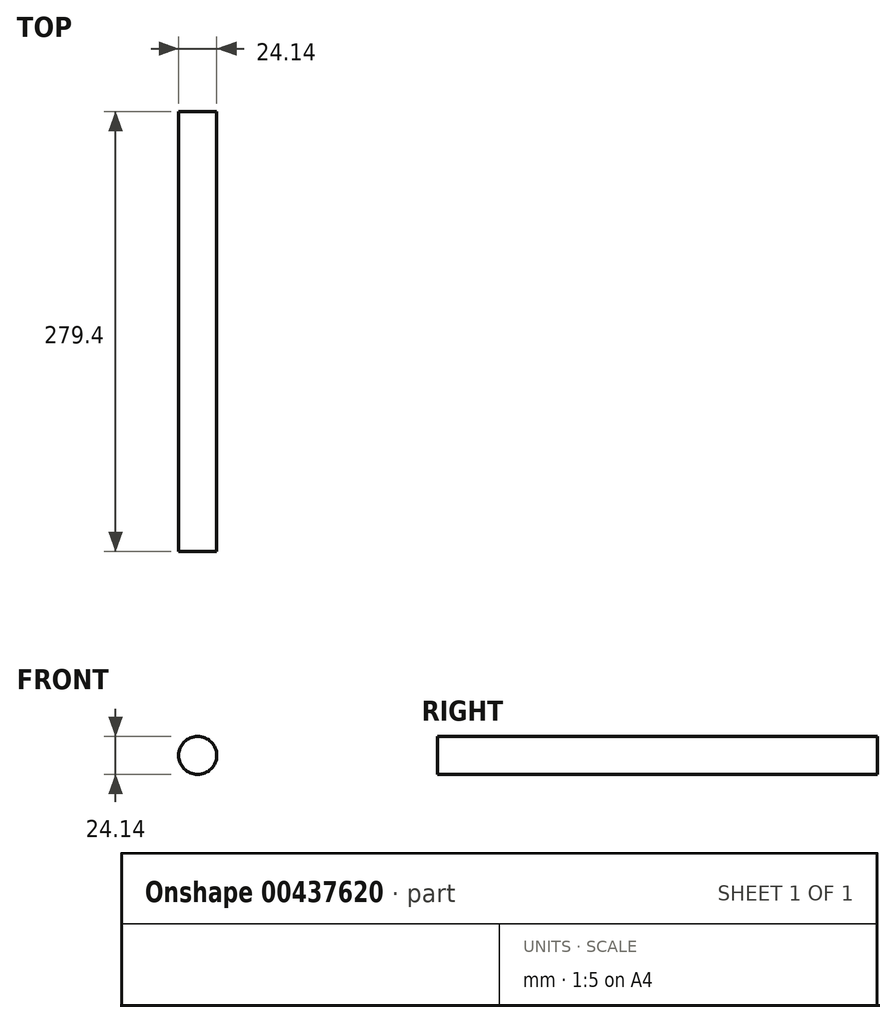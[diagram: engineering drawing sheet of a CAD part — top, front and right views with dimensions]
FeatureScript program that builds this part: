
annotation { "Feature Type Name" : "Feature", "Feature Type Description" : "" }
export const myFeature = defineFeature(function(context is Context, id is Id, definition is map)
    precondition{}
    {
        {
            var Q0;
            Q0=qCreatedBy(makeId("Front.planeOp"),FACE);
            var sketch = newSketch(context, id + "F0", { "sketchPlane" : qUnion([Q0])});
            skCircle(sketch, "E0", {"center": v(0, 0) * mm, "radius": 12.07 * mm});
            skSolve(sketch);
        }
        {
            var Q0;
            Q0 = qSketchRegion(id + "F0", true);
            extrude(context, id + "F1", {"entities" : qUnion([Q0]), "depth" : 279.4 * mm});
        }
    });
